# Revit family: polusfera_d60
name_source: partatom
category: Антураж
revit_build: Autodesk Revit 2017 (Build: 20160225_1515(x64)
units: mm (PartAtom-declared; Revit-internal decimal feet)

## family parameters
Всегда вертикально = Да
Источник визуального образа = Геометрия семейства
На основе рабочей плоскости = Нет
Общий = Нет
При загрузке вырезать с полостями = Нет
Точка расчета площади = Нет

## types (9) — shared parameters
Диаметр = 600 мм
Наименование = Полусфера "D60"
Объем бетона = 0.05 м³
Производитель = ГК Очаковский комбинат ЖБИ
zero-valued in all types: Высота

## per-type parameters (varying)
| type | URL | Материал |
| "D60" Белый |  | Очаковский_Белый |
| "D60" Белый шелк |  | Очаковский_Белый_Шелк |
| "D60" Крымский берег |  | Очаковский_Крымский_берег |
| "D60" Московский гравий |  | Очаковский_Московский_гравий |
| "D60" Морская соль |  | Очаковский_Морская_соль |
| "D60" Светло-серый |  | Очаковский_Светло-серый |
| "D60" Черный шелк |  | Очаковский_Черный_шелк |
| "D60" Черный глянец |  | Очаковский_Черный_глянец |
| "D60" Шахматка | http://file-system.ru | Очаковский_Шахматка |

## geometry (parser evidence)
native form markers: Blend x159
no freeform markers — native parametric forms only
